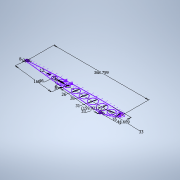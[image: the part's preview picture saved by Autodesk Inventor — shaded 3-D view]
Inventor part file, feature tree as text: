
AUTODESK INVENTOR PART (.ipt)
format: ipt  version: 2022 (Build 260153000, 153)  size: 193,024 bytes
history: native  units: mm
features: sketch x1
ambient origin geometry x8: Origin, YZ Plane, XZ Plane, XY Plane, X Axis, Y Axis, Z Axis, Center Point
feature tree (1):
  sketch  "Sketch1"  dims[d8=159.921431mm d26=5.0mm d27=5.0mm d31=34.456mm d36=5.0mm d37=5.0mm d50=368.759386mm d51=16.0mm d52=28.0mm d53=31.0mm d54=26.0mm d57=16.0mm d59=33.0mm d65=44.669323mm d66=25.0mm d67=12.0mm d68=160.0mm d69=8.0mm d70=23.0mm d71=8.0mm d73=16.0mm d77=2.0mm d78=33.0mm d79=8.0mm]
